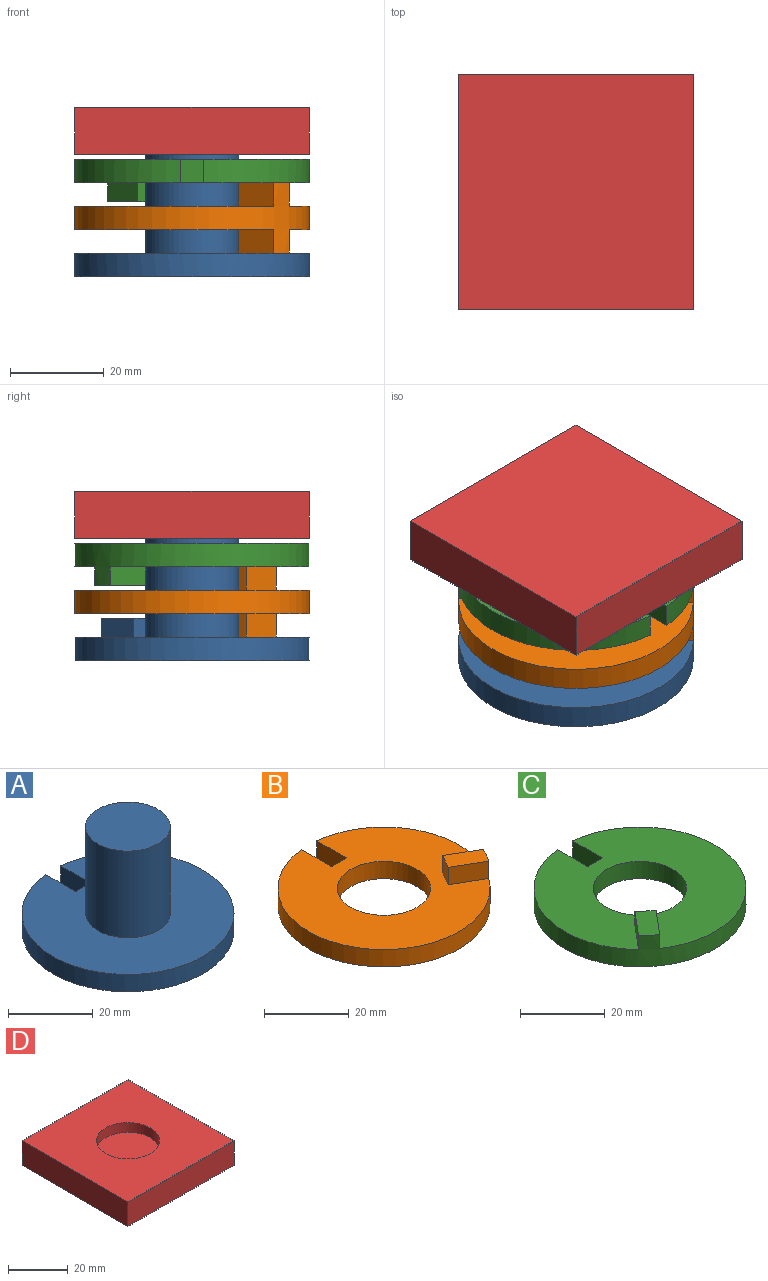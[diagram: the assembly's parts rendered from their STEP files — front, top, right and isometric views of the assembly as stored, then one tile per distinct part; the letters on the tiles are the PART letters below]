
ASSEMBLY  parts=4 mates=3
PART A: 12 faces, bbox 50x49.9x30 mm
  f0: cylinder r=25mm len=50mm, axis (0,0,-1), area 780.4mm2, adj f1,f3,f4,f5,f9,f10,f11
  f1: plane 9.87x5mm, normal (-1,0,0), area 49.4mm2, adj f0,f2,f4,f5
  f2: plane 5x5mm, normal (0,1,0), area 25mm2, adj f1,f3,f4,f5
  f3: plane 9.87x5mm, normal (1,0,0), area 49.4mm2, adj f0,f2,f4,f5
  f4: plane 50x49.87mm, normal (0,0,1), area 1549.8mm2, adj f0,f1,f2,f3,f6,f8,f9,f10
  f5: plane 50x49.87mm, normal (0,0,-1), area 1913.7mm2, adj f0,f1,f2,f3
  f6: cylinder r=10mm len=25mm, axis (0,0,-1), area 1570.8mm2, adj f4,f7
  f7: plane 20x20mm, normal (0,0,1), area 314.2mm2, adj f6
  f8: plane 4x3.54mm, normal (-0.71,-0.71,0), area 20mm2, adj f4,f9,f10,f11
  f9: plane 6.98x6.98mm, normal (0.71,-0.71,0), area 39.5mm2, adj f0,f4,f8,f11
  f10: plane 6.98x6.98mm, normal (-0.71,0.71,0), area 39.5mm2, adj f0,f4,f8,f11
  f11: plane 10.52x10.52mm, normal (0,0,1), area 49.8mm2, adj f0,f8,f9,f10
PART B: 15 faces, bbox 50x49.9x15 mm
  f0: plane 9.87x5mm, normal (-1,0,0), area 49.4mm2, adj f1,f4,f5,f6
  f1: plane 5x5mm, normal (0,1,0), area 25mm2, adj f0,f2,f5,f6
  f2: plane 9.87x5mm, normal (1,0,0), area 49.4mm2, adj f1,f4,f5,f6
  f3: cylinder r=11mm len=22mm, axis (0,0,-1), area 345.6mm2, adj f5,f6
  f4: cylinder r=25mm len=50mm, axis (0,0,-1), area 810.4mm2, adj f0,f2,f5,f6,f7,f8,f9,f12
  f5: plane 50x49.87mm, normal (0,0,1), area 1483.8mm2, adj f0,f1,f2,f3,f4,f11,f12,f13
  f6: plane 50x49.87mm, normal (0,0,-1), area 1483.8mm2, adj f0,f1,f2,f3,f4,f8,f9,f10
  f7: plane 11.05x9.27mm, normal (0,0,-1), area 49.8mm2, adj f4,f8,f9,f10
  f8: plane 8.55x5mm, normal (0.5,0.87,0), area 49.4mm2, adj f4,f6,f7,f10
  f9: plane 8.55x5mm, normal (-0.5,-0.87,0), area 49.4mm2, adj f4,f6,f7,f10
  f10: plane 5x4.33mm, normal (-0.87,0.5,0), area 25mm2, adj f6,f7,f8,f9
  f11: plane 5x4.33mm, normal (-0.87,0.5,0), area 25mm2, adj f5,f12,f13,f14
  f12: plane 8.55x5mm, normal (-0.5,-0.87,0), area 49.4mm2, adj f4,f5,f11,f14
  f13: plane 8.55x5mm, normal (0.5,0.87,0), area 49.4mm2, adj f4,f5,f11,f14
  f14: plane 11.05x9.27mm, normal (0,0,1), area 49.8mm2, adj f4,f11,f12,f13
PART C: 11 faces, bbox 50x49.9x9 mm
  f0: cylinder r=25mm len=50mm, axis (0,0,-1), area 780.4mm2, adj f1,f4,f5,f6,f7,f8,f10
  f1: plane 9.87x5mm, normal (-1,0,0), area 49.4mm2, adj f0,f2,f5,f6
  f2: plane 5x5mm, normal (0,1,0), area 25mm2, adj f1,f4,f5,f6
  f3: cylinder r=11mm len=22mm, axis (0,0,-1), area 345.6mm2, adj f5,f6
  f4: plane 9.87x5mm, normal (1,0,0), area 49.4mm2, adj f0,f2,f5,f6
  f5: plane 50x49.87mm, normal (0,0,1), area 1483.8mm2, adj f0,f1,f2,f3,f4,f7,f8,f9
  f6: plane 50x49.87mm, normal (0,0,-1), area 1533.6mm2, adj f0,f1,f2,f3,f4
  f7: plane 7.56x6.35mm, normal (-0.77,0.64,0), area 39.5mm2, adj f0,f5,f9,f10
  f8: plane 7.56x6.35mm, normal (0.77,-0.64,0), area 39.5mm2, adj f0,f5,f9,f10
  f9: plane 4x3.83mm, normal (0.64,0.77,0), area 20mm2, adj f5,f7,f8,f10
  f10: plane 10.78x10.18mm, normal (0,0,1), area 49.8mm2, adj f0,f7,f8,f9
PART D: 8 faces, bbox 50x50x10 mm
  f0: plane 50x10mm, normal (0,1,0), area 500mm2, adj f1,f4,f5,f6
  f1: plane 50x10mm, normal (-1,0,0), area 500mm2, adj f0,f2,f5,f6
  f2: plane 50x10mm, normal (0,-1,0), area 500mm2, adj f1,f4,f5,f6
  f3: cylinder r=10.5mm len=21mm, axis (0,0,-1), area 263.9mm2, adj f5,f7
  f4: plane 50x10mm, normal (1,0,0), area 500mm2, adj f0,f2,f5,f6
  f5: plane 50x50mm, normal (0,0,1), area 2153.6mm2, adj f0,f1,f2,f3,f4
  f6: plane 50x50mm, normal (0,0,-1), area 2500mm2, adj f0,f1,f2,f4
  f7: plane 21x21mm, normal (0,0,1), area 346.4mm2, adj f3
PLACE A t=(-4.8,-53.96,32.12)mm
PLACE B rot(axis=(0,0,-1),10deg) t=(-4.8,-53.96,42.12)mm
PLACE C rot(axis=(-1,0,0),180deg) t=(-4.8,-53.96,57.06)mm
PLACE D rot(axis=(-1,0,0),180deg) t=(-4.8,-53.96,68.12)mm
MATE cylindrical A.f6 <-> D.f3  axis (0,0,-1) through (-4.8,-53.96,49.62)mm
MATE cylindrical A.f6 <-> C.f3  axis (0,0,-1) through (-4.8,-53.96,49.62)mm
MATE cylindrical A.f6 <-> B.f3  axis (0,0,-1) through (-4.8,-53.96,49.62)mm
